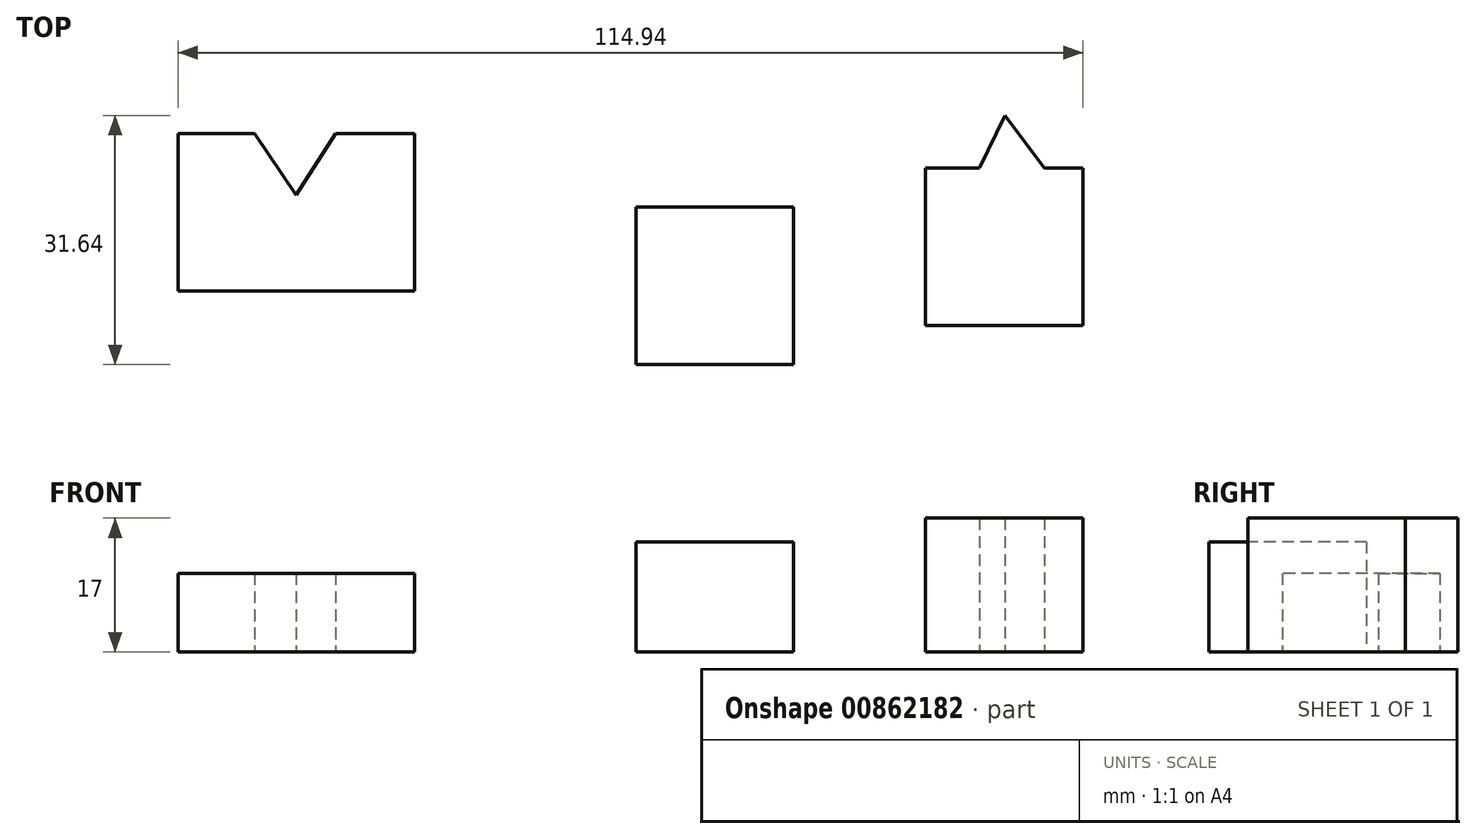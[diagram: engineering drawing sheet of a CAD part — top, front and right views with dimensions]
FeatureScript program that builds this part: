
annotation { "Feature Type Name" : "Feature", "Feature Type Description" : "" }
export const myFeature = defineFeature(function(context is Context, id is Id, definition is map)
    precondition{}
    {
        {
            var Q0;
            Q0=qCreatedBy(makeId("Top.planeOp"),FACE);
            var sketch = newSketch(context, id + "F0", { "sketchPlane" : qUnion([Q0])});
            skLineSegment(sketch, "E0.bottom", {"start": v(-10.55, 4.03) * mm, "end": v(9.45, 4.03) * mm});
            skLineSegment(sketch, "E0.top", {"start": v(-10.55, -15.97) * mm, "end": v(9.45, -15.97) * mm});
            skLineSegment(sketch, "E0.left", {"start": v(-10.55, 4.03) * mm, "end": v(-10.55, -15.97) * mm});
            skLineSegment(sketch, "E0.right", {"start": v(9.45, 4.03) * mm, "end": v(9.45, -15.97) * mm});
            skSolve(sketch);
        }
        {
            var Q0;
            Q0=makeQuery(id+"F0.imprint","IMPRINT",FACE,{"disambiguationData":[TD([[makeQuery(id+"F0.imprint","IMPRINT",EDGE,{"derivedFrom":sQuery(id+"F0.wireOp",EDGE,"E0.bottom")}),-1.0]])]});
            extrude(context, id + "F1", {"entities" : qUnion([Q0]), "depth" : 14 * mm, "offsetDistance" : 25 * mm});
        }
        {
            var Q0;
            Q0=qCreatedBy(makeId("Top.planeOp"),FACE);
            var sketch = newSketch(context, id + "F2", { "sketchPlane" : qUnion([Q0])});
            skLineSegment(sketch, "E1.bottom", {"start": v(26.2, 9) * mm, "end": v(33.07, 9) * mm});
            skLineSegment(sketch, "E1.top", {"start": v(26.2, -11) * mm, "end": v(46.2, -11) * mm});
            skLineSegment(sketch, "E1.left", {"start": v(26.2, 9) * mm, "end": v(26.2, -11) * mm});
            skLineSegment(sketch, "E1.right", {"start": v(46.2, 9) * mm, "end": v(46.2, -11) * mm});
            skLineSegment(sketch, "E2", {"start": v(41.28, 9) * mm, "end": v(36.28, 15.67) * mm});
            skLineSegment(sketch, "E3", {"start": v(36.28, 15.67) * mm, "end": v(33.07, 9) * mm});
            skLineSegment(sketch, "E4.trimOffspring", {"start": v(41.28, 9) * mm, "end": v(46.2, 9) * mm});
            skSolve(sketch);
        }
        {
            var Q0;
            Q0=makeQuery(id+"F2.imprint","IMPRINT",FACE,{"disambiguationData":[TD([[makeQuery(id+"F2.imprint","IMPRINT",EDGE,{"derivedFrom":sQuery(id+"F2.wireOp",EDGE,"E1.bottom")}),-1.0]])]});
            extrude(context, id + "F3", {"entities" : qUnion([Q0]), "depth" : 17 * mm, "offsetDistance" : 25 * mm});
        }
        {
            var Q0;
            Q0=qCreatedBy(makeId("Top.planeOp"),FACE);
            var sketch = newSketch(context, id + "F4", { "sketchPlane" : qUnion([Q0])});
            skLineSegment(sketch, "E5.bottom", {"start": v(-68.73, 13.39) * mm, "end": v(-59.03, 13.39) * mm});
            skLineSegment(sketch, "E5.top", {"start": v(-68.73, -6.61) * mm, "end": v(-38.73, -6.61) * mm});
            skLineSegment(sketch, "E5.left", {"start": v(-68.73, 13.39) * mm, "end": v(-68.73, -6.61) * mm});
            skLineSegment(sketch, "E5.right", {"start": v(-38.73, 13.39) * mm, "end": v(-38.73, -6.61) * mm});
            skLineSegment(sketch, "E6", {"start": v(-59.03, 13.39) * mm, "end": v(-53.73, 5.58) * mm});
            skPoint(sketch, "E6.endSnap0", {"position": v(-53.73, 13.39) * mm});
            skLineSegment(sketch, "E7", {"start": v(-53.73, 5.58) * mm, "end": v(-48.7, 13.39) * mm});
            skLineSegment(sketch, "E8.trimOffspring", {"start": v(-48.7, 13.39) * mm, "end": v(-38.73, 13.39) * mm});
            skSolve(sketch);
        }
        {
            var Q0;
            Q0=makeQuery(id+"F4.imprint","IMPRINT",FACE,{"disambiguationData":[TD([[makeQuery(id+"F4.imprint","IMPRINT",EDGE,{"derivedFrom":sQuery(id+"F4.wireOp",EDGE,"E5.bottom")}),-1.0]])]});
            extrude(context, id + "F5", {"entities" : qUnion([Q0]), "depth" : 10 * mm, "offsetDistance" : 25 * mm});
        }
    });
